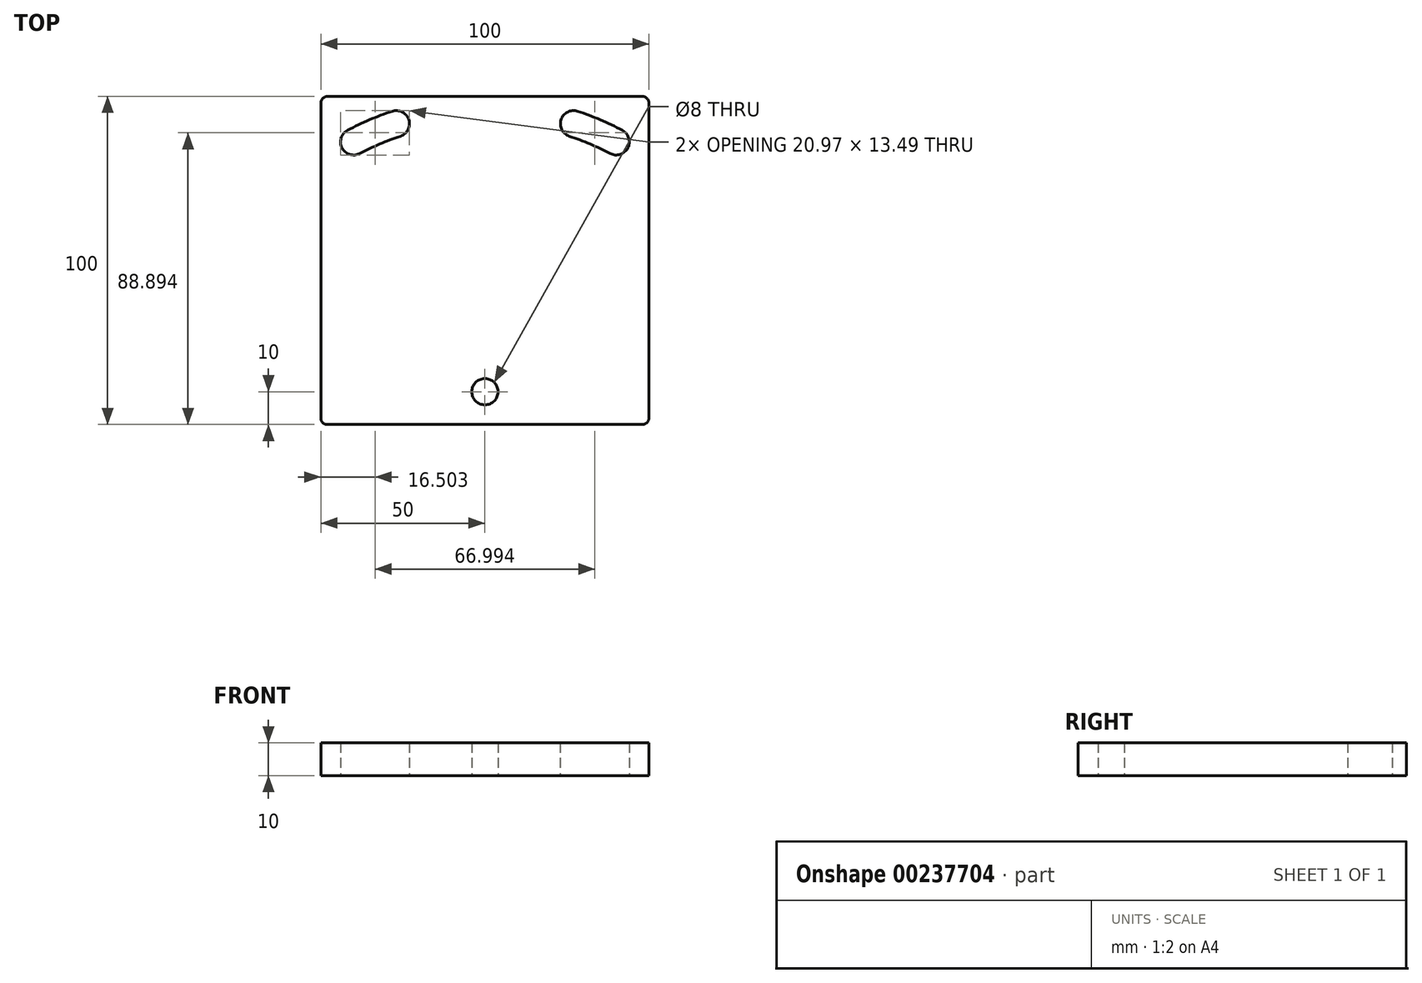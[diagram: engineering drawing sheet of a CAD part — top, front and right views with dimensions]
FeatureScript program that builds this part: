
annotation { "Feature Type Name" : "Feature", "Feature Type Description" : "" }
export const myFeature = defineFeature(function(context is Context, id is Id, definition is map)
    precondition{}
    {
        {
            var Q0;
            Q0=qCreatedBy(makeId("Top.planeOp"),FACE);
            var sketch = newSketch(context, id + "F0", { "sketchPlane" : qUnion([Q0])});
            skLineSegment(sketch, "E0.bottom", {"start": v(48, 50) * mm, "end": v(-48, 50) * mm});
            skLineSegment(sketch, "E0.top", {"start": v(48, -50) * mm, "end": v(-48, -50) * mm});
            skLineSegment(sketch, "E0.left", {"start": v(50, 48) * mm, "end": v(50, -48) * mm});
            skLineSegment(sketch, "E0.right", {"start": v(-50, 48) * mm, "end": v(-50, -48) * mm});
            skPoint(sketch, "E0.middle", {"position": v(0, 0) * mm});
            skPoint(sketch, "E1.visualSharp", {"position": v(-50, 50) * mm});
            skArc(sketch, "E1.filletArc", {"start": v(-48, 50) * mm, "mid": v(-49.41, 49.41) * mm, "end": v(-50, 48) * mm});
            skPoint(sketch, "E2.visualSharp", {"position": v(50, 50) * mm});
            skArc(sketch, "E2.filletArc", {"start": v(50, 48) * mm, "mid": v(49.41, 49.41) * mm, "end": v(48, 50) * mm});
            skPoint(sketch, "E3.visualSharp", {"position": v(50, -50) * mm});
            skArc(sketch, "E3.filletArc", {"start": v(48, -50) * mm, "mid": v(49.41, -49.41) * mm, "end": v(50, -48) * mm});
            skPoint(sketch, "E4.visualSharp", {"position": v(-50, -50) * mm});
            skArc(sketch, "E4.filletArc", {"start": v(-50, -48) * mm, "mid": v(-49.41, -49.41) * mm, "end": v(-48, -50) * mm});
            skCircle(sketch, "E5", {"center": v(0, -40) * mm, "radius": 4 * mm});
            skArc(sketch, "E6", {"start": v(-28.26, 45.45) * mm, "mid": v(-35.18, 42.84) * mm, "end": v(-41.86, 39.67) * mm});
            skArc(sketch, "E7", {"start": v(-25.74, 37.85) * mm, "mid": v(-32.05, 35.48) * mm, "end": v(-38.14, 32.6) * mm});
            skArc(sketch, "E8", {"start": v(-25.74, 37.85) * mm, "mid": v(-23.2, 42.9) * mm, "end": v(-28.26, 45.45) * mm});
            skArc(sketch, "E9", {"start": v(-41.86, 39.67) * mm, "mid": v(-43.54, 34.27) * mm, "end": v(-38.14, 32.6) * mm});
            skArc(sketch, "E10", {"start": v(28.26, 45.45) * mm, "mid": v(23.2, 42.9) * mm, "end": v(25.74, 37.85) * mm});
            skArc(sketch, "E11", {"start": v(38.14, 32.6) * mm, "mid": v(43.54, 34.27) * mm, "end": v(41.86, 39.67) * mm});
            skArc(sketch, "E12.trimOffspring", {"start": v(38.14, 32.6) * mm, "mid": v(32.05, 35.48) * mm, "end": v(25.74, 37.85) * mm});
            skArc(sketch, "E13.trimOffspring", {"start": v(41.86, 39.67) * mm, "mid": v(35.18, 42.84) * mm, "end": v(28.26, 45.45) * mm});
            skPoint(sketch, "E14", {"position": v(0, 20) * mm});
            skSolve(sketch);
        }
        {
            var Q0;
            Q0=makeQuery(id+"F0.imprint","IMPRINT",FACE,{"disambiguationData":[TD([[makeQuery(id+"F0.imprint","IMPRINT",EDGE,{"derivedFrom":sQuery(id+"F0.wireOp",EDGE,"E0.bottom")}),1.0]])]});
            extrude(context, id + "F1", {"entities" : qUnion([Q0]), "depth" : 10 * mm});
        }
    });
